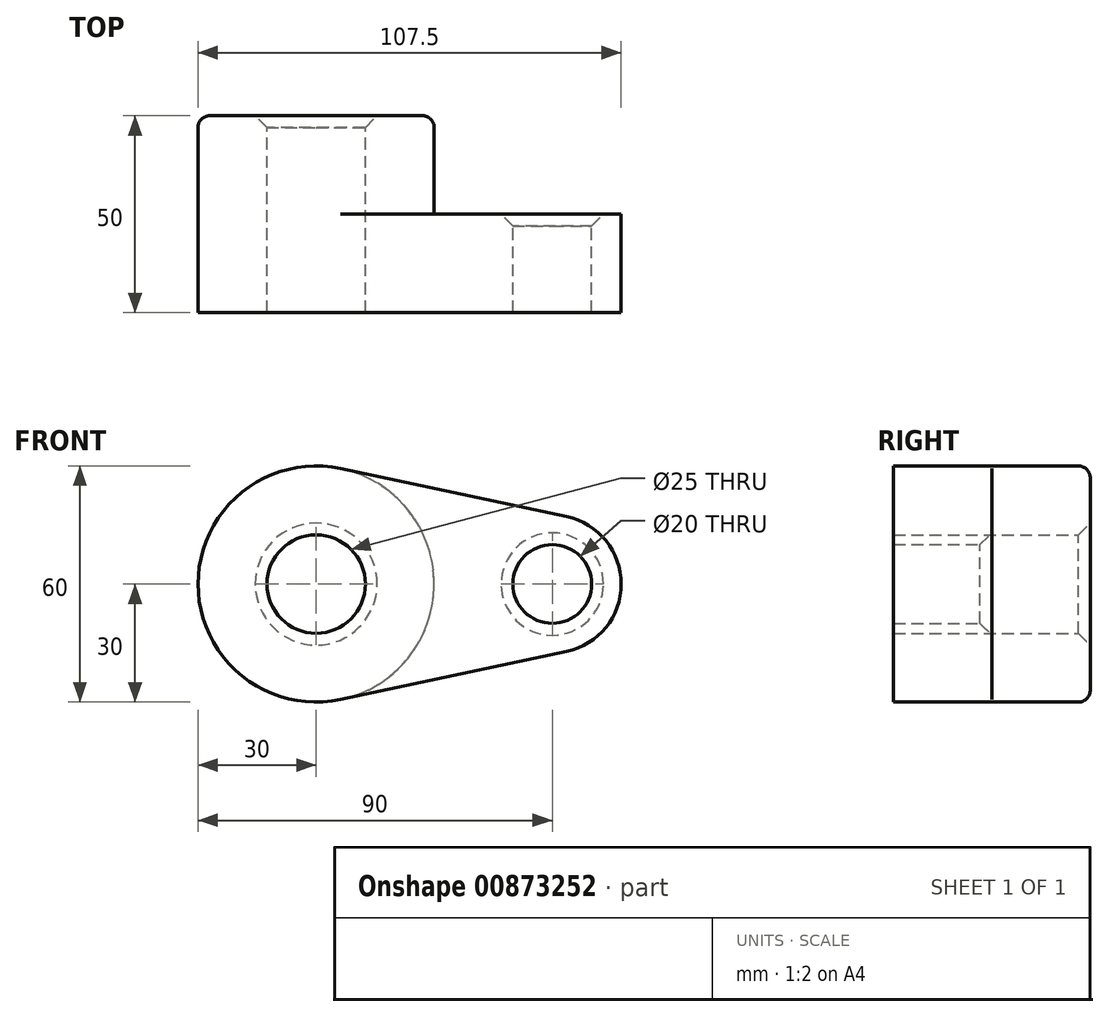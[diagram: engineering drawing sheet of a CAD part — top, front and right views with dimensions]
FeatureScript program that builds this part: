
annotation { "Feature Type Name" : "Feature", "Feature Type Description" : "" }
export const myFeature = defineFeature(function(context is Context, id is Id, definition is map)
    precondition{}
    {
        {
            var Q0;
            Q0=qCreatedBy(makeId("Front.planeOp"),FACE);
            var sketch = newSketch(context, id + "F0", { "sketchPlane" : qUnion([Q0])});
            skCircle(sketch, "E0", {"center": v(0, 0) * mm, "radius": 30 * mm});
            skCircle(sketch, "E1", {"center": v(60, 0) * mm, "radius": 17.5 * mm});
            skCircle(sketch, "E2", {"center": v(0, 0) * mm, "radius": 12.5 * mm});
            skCircle(sketch, "E3", {"center": v(60, 0) * mm, "radius": 10 * mm});
            skLineSegment(sketch, "E4", {"start": v(6.25, 29.34) * mm, "end": v(63.65, 17.12) * mm});
            skLineSegment(sketch, "E5", {"start": v(6.25, -29.34) * mm, "end": v(63.65, -17.12) * mm});
            skSolve(sketch);
        }
        {
            var Q0;
            Q0 = qSketchRegion(id + "F0", true);
            extrude(context, id + "F1", {"entities" : qUnion([Q0]), "depth" : 25 * mm, "offsetDistance" : 25 * mm});
        }
        {
            var Q0;
            Q0=makeQuery(id+"F0.imprint","IMPRINT",FACE,{"disambiguationData":[TD([[makeQuery(id+"F0.imprint","IMPRINT",EDGE,{"derivedFrom":sQuery(id+"F0.wireOp",EDGE,"E2")}),-1.0]])]});
            extrude(context, id + "F2", {"entities" : qUnion([Q0]), "operationType" : NewBodyOperationType.ADD, "oppositeDirection" : true, "depth" : 25 * mm, "offsetDistance" : 25 * mm});
        }
        {
            var Q0;
            Q0=makeQuery(id+"F2.opExtrude","CAP_EDGE",EDGE,{"disambiguationData":[OSD([sQuery(id+"F0.wireOp",EDGE,"E0")])],"isStart":false});
            fillet(context, id + "F3", {"entities" : qUnion([Q0]), "radius" : 3 * mm, "tangentPropagation" : true, "allowEdgeOverflow" : false});
        }
        {
            var Q0;
            Q0=makeQuery(id+"F2.opExtrude","CAP_EDGE",EDGE,{"disambiguationData":[OSD([sQuery(id+"F0.wireOp",EDGE,"E2")])],"isStart":false});
            var Q1;
            Q1=makeQuery(id+"F1.opExtrude","CAP_EDGE",EDGE,{"disambiguationData":[OSD([sQuery(id+"F0.wireOp",EDGE,"E3")])],"isStart":true});
            chamfer(context, id + "F4", {"entities" : qUnion([Q0, Q1]), "width" : 3 * mm, "tangentPropagation" : true});
        }
    });
